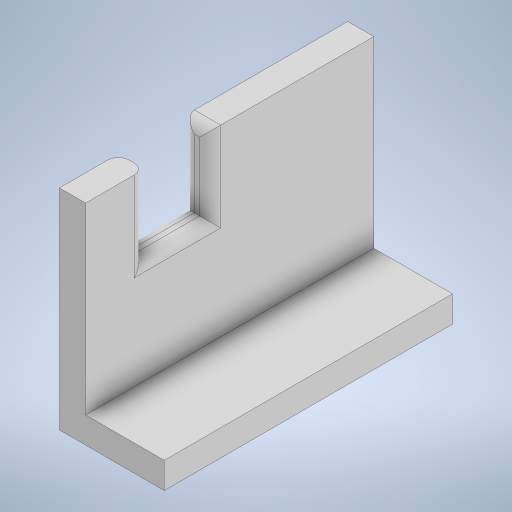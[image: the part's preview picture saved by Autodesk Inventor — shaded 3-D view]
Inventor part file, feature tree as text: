
AUTODESK INVENTOR PART (.ipt)
format: ipt  version: 2023 (Build 270158000, 158)  size: 227,328 bytes
history: native  units: in
note: dims shown in document units (in); Inventor stores cm internally (conversion verified against a paired STEP export)
features: extrude x2, sketch x2, fillet x1
ambient origin geometry x8: Origin, YZ Plane, XZ Plane, XY Plane, X Axis, Y Axis, Z Axis, Center Point
bodies: Solid1 (feature_tree)
feature tree (5):
  extrude  "Extrusion1"  Depth=0.6299in
  extrude  "Extrusion3"  Depth=0.8661in TaperAngle=0.0deg
  fillet  "Fillet1"  Radius=0.1969in
  sketch  "Sketch1"  dims[d0=0.0787in d1=0.6299in]
  sketch  "Sketch3"  dims[d2=0.2362in d3=0.8661in d4=0.0in d9=0.1969in d10=0.2362in d11=0.3937in d12=0.0in d13=0.0315in]
